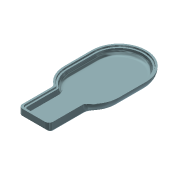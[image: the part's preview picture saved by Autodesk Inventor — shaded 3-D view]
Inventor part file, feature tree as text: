
AUTODESK INVENTOR PART (.ipt)
format: ipt  version: 2022.1 (Build 261234020, 234B)  size: 675,328 bytes
history: native  units: mm
features: fillet x7, extrude x6, sketch x5, other x1, projected_geometry x1
ambient origin geometry x8: Origin, YZ Plane, XZ Plane, XY Plane, X Axis, Y Axis, Z Axis, Center Point
bodies: Solid1 (feature_tree)
feature tree (20):
  sketch  "Sketch1"  dims[d0=70.0mm d1=70.0mm]
  extrude  "Extrusion1"  Depth=70.0mm
  extrude  "Extrusion2"  Depth=80.0mm
  extrude  "Extrusion8"  Depth=10.0mm
  fillet  "Fillet2"  Radius=20.0mm
  fillet  "Fillet3"  Radius=40.0mm
  extrude  "Extrusion9"  Depth=10.0mm
  extrude  "Extrusion12"  Depth=10.0mm TaperAngle=0.0deg
  extrude  "Extrusion13"  Depth=10.0mm TaperAngle=0.0deg
  fillet  "Fillet4"  Radius=5.0mm
  fillet  "Fillet5"  Radius=5.0mm
  fillet  "Fillet6"  Radius=10.0mm
  fillet  "Fillet7"  Radius=15.0mm
  fillet  "Fillet8"  Radius=6.0mm
  other  "Lip3"
  sketch  "Sketch5"  dims[d2=40.0mm d3=80.0mm]
  sketch  "Sketch6"  dims[d4=45.0mm d5=10.0mm d6=20.0mm d7=40.0mm]
  sketch  "Sketch9"  dims[d8=10.0mm d9=10.0mm]
  sketch  "Sketch10"  dims[d10=20.0mm d11=15.0mm d12=0.0mm d13=15.0mm d14=0.0mm d34=5.0mm d35=5.0mm d36=10.0mm d37=0.0mm d38=15.0mm d39=6.0mm d46=45.0mm d47=45.0mm d48=12.5mm d49=0.0mm d57=5.0mm d58=17.5mm d59=17.5mm d60=10.0mm d61=0.0mm d62=60.0mm d63=0.0mm d64=6.0mm d65=3.0mm d66=5.0mm d67=6.0mm d68=3.0mm d69=2.0mm d70=2.5mm d71=0.0mm d72=0.0mm d73=1.745329mm d74=0.0mm d18=0.0mm d19=0.0mm d20=0.0mm d21=0.0mm d50=0.5mm d51=0.872665mm d52=0.5mm d53=0.872665mm d55=0.0mm d56=0.0mm]
  projected_geometry  "Projected Loop2"
